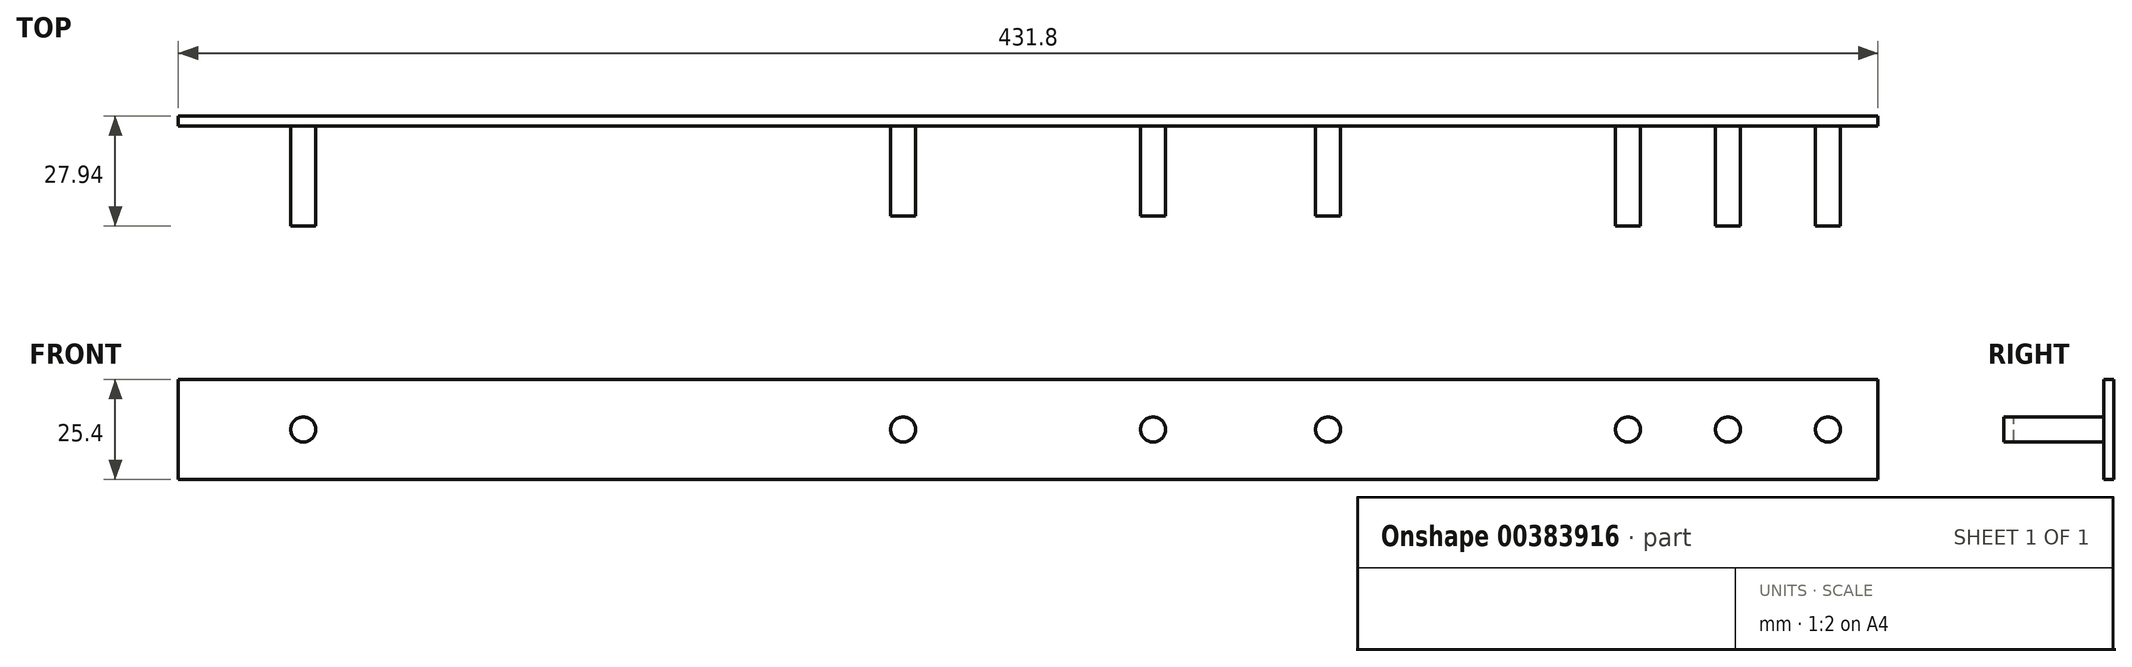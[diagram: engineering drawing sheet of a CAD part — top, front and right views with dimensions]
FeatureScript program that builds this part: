
annotation { "Feature Type Name" : "Feature", "Feature Type Description" : "" }
export const myFeature = defineFeature(function(context is Context, id is Id, definition is map)
    precondition{}
    {
        {
            var Q0;
            Q0=qCreatedBy(makeId("Front.planeOp"),FACE);
            var sketch = newSketch(context, id + "F0", { "sketchPlane" : qUnion([Q0])});
            skLineSegment(sketch, "E0.bottom", {"start": v(-88.9, 12.7) * mm, "end": v(88.9, 12.7) * mm});
            skLineSegment(sketch, "E0.top", {"start": v(-88.9, -12.7) * mm, "end": v(88.9, -12.7) * mm});
            skLineSegment(sketch, "E0.left", {"start": v(-88.9, 12.7) * mm, "end": v(-88.9, -12.7) * mm});
            skLineSegment(sketch, "E0.right", {"start": v(88.9, 12.7) * mm, "end": v(88.9, -12.7) * mm});
            skPoint(sketch, "E0.middle", {"position": v(0, 0) * mm});
            skSolve(sketch);
        }
        {
            var Q0;
            Q0=makeQuery(id+"F0.imprint","IMPRINT",FACE,{"disambiguationData":[TD([[makeQuery(id+"F0.imprint","IMPRINT",EDGE,{"derivedFrom":sQuery(id+"F0.wireOp",EDGE,"E0.bottom")}),-1.0]])]});
            extrude(context, id + "F1", {"entities" : qUnion([Q0]), "depth" : 2.54 * mm});
        }
        {
            var Q0;
            Q0=qCreatedBy(makeId("Front.planeOp"),FACE);
            var sketch = newSketch(context, id + "F2", { "sketchPlane" : qUnion([Q0])});
            skCircle(sketch, "E1", {"center": v(-31.75, 0) * mm, "radius": 3.18 * mm});
            skCircle(sketch, "E2.MirrorC", {"center": v(31.75, 0) * mm, "radius": 3.18 * mm});
            skCircle(sketch, "E3", {"center": v(76.2, 0) * mm, "radius": 3.18 * mm});
            skLineSegment(sketch, "E4", {"start": v(-31.75, 0) * mm, "end": v(-31.75, 53.04) * mm, "construction": true});
            skSolve(sketch);
        }
        {
            var Q0;
            Q0=makeQuery(id+"F2.imprint","IMPRINT",FACE,{"disambiguationData":[TD([[makeQuery(id+"F2.imprint","IMPRINT",EDGE,{"derivedFrom":sQuery(id+"F2.wireOp",EDGE,"E1")}),1.0]])]});
            var Q1;
            Q1=makeQuery(id+"F2.imprint","IMPRINT",FACE,{"disambiguationData":[TD([[makeQuery(id+"F2.imprint","IMPRINT",EDGE,{"derivedFrom":sQuery(id+"F2.wireOp",EDGE,"E2.MirrorC")}),-1.0]])]});
            extrude(context, id + "F3", {"entities" : qUnion([Q0, Q1]), "operationType" : NewBodyOperationType.ADD, "depth" : 25.4 * mm});
        }
        {
            var Q0;
            Q0 = qSketchRegion(id + "F2", true);
            extrude(context, id + "F4", {"entities" : qUnion([Q0]), "operationType" : NewBodyOperationType.ADD, "depth" : 25.4 * mm});
        }
        {
            var Q0;
            Q0=makeQuery(id+"F1.opExtrude","SWEPT_FACE",FACE,{"disambiguationData":[OSD([sQuery(id+"F0.wireOp",EDGE,"E0.left")])]});
            extrude(context, id + "F5", {"entities" : qUnion([Q0]), "operationType" : NewBodyOperationType.ADD, "depth" : 127 * mm});
        }
        {
            var Q0;
            {var subQ0=sQuery(id+"F0.wireOp",EDGE,"E0.left");Q0=makeQuery(id+"F5.boolean.opBoolean","MERGE",FACE,{"derivedFrom":[makeQuery(id+"F1.opExtrude","CAP_FACE",FACE,{"disambiguationData":[OSD([sQuery(id+"F0.wireOp",EDGE,"E0.bottom"),sQuery(id+"F0.wireOp",EDGE,"E0.top"),subQ0,sQuery(id+"F0.wireOp",EDGE,"E0.right")])],"isStart":false}),makeQuery(id+"F5.opExtrude","SWEPT_FACE",FACE,{"disambiguationData":[OSD([subQ0]),TDD([makeQuery(id+"F1.opExtrude","CAP_EDGE",EDGE,{"disambiguationData":[OSD([subQ0])],"isStart":false})])]})]});}
            var sketch = newSketch(context, id + "F6", { "sketchPlane" : qUnion([Q0])});
            skCircle(sketch, "E5", {"center": v(-184.15, 0) * mm, "radius": 3.18 * mm});
            skSolve(sketch);
        }
        {
            var Q0;
            Q0=makeQuery(id+"F6.imprint","IMPRINT",FACE,{"disambiguationData":[TD([[makeQuery(id+"F6.imprint","IMPRINT",EDGE,{"derivedFrom":sQuery(id+"F6.wireOp",EDGE,"E5")}),1.0]])]});
            extrude(context, id + "F7", {"entities" : qUnion([Q0]), "operationType" : NewBodyOperationType.ADD, "depth" : 25.4 * mm});
        }
        {
            var Q0;
            Q0=makeQuery(id+"F1.opExtrude","SWEPT_FACE",FACE,{"disambiguationData":[OSD([sQuery(id+"F0.wireOp",EDGE,"E0.right")])]});
            extrude(context, id + "F8", {"entities" : qUnion([Q0]), "operationType" : NewBodyOperationType.ADD, "depth" : 127 * mm});
        }
        {
            var Q0;
            {var subQ0=sQuery(id+"F0.wireOp",EDGE,"E0.right");var subQ1=sQuery(id+"F0.wireOp",EDGE,"E0.left");Q0=makeQuery(id+"F8.boolean.opBoolean","MERGE",FACE,{"derivedFrom":[makeQuery(id+"F5.boolean.opBoolean","MERGE",FACE,{"derivedFrom":[makeQuery(id+"F1.opExtrude","CAP_FACE",FACE,{"disambiguationData":[OSD([sQuery(id+"F0.wireOp",EDGE,"E0.bottom"),sQuery(id+"F0.wireOp",EDGE,"E0.top"),subQ1,subQ0])],"isStart":false}),makeQuery(id+"F5.opExtrude","SWEPT_FACE",FACE,{"disambiguationData":[OSD([subQ1]),TDD([makeQuery(id+"F1.opExtrude","CAP_EDGE",EDGE,{"disambiguationData":[OSD([subQ1])],"isStart":false})])]})]}),makeQuery(id+"F8.opExtrude","SWEPT_FACE",FACE,{"disambiguationData":[OSD([subQ0]),TDD([makeQuery(id+"F1.opExtrude","CAP_EDGE",EDGE,{"disambiguationData":[OSD([subQ0])],"isStart":false})])]})]});}
            var sketch = newSketch(context, id + "F9", { "sketchPlane" : qUnion([Q0])});
            skCircle(sketch, "E6", {"center": v(152.4, 0) * mm, "radius": 3.18 * mm});
            skCircle(sketch, "E7", {"center": v(177.8, 0) * mm, "radius": 3.18 * mm});
            skCircle(sketch, "E8", {"center": v(203.2, 0) * mm, "radius": 3.18 * mm});
            skSolve(sketch);
        }
        {
            var Q0;
            Q0=makeQuery(id+"F9.imprint","IMPRINT",FACE,{"disambiguationData":[TD([[makeQuery(id+"F9.imprint","IMPRINT",EDGE,{"derivedFrom":sQuery(id+"F9.wireOp",EDGE,"E6")}),1.0]])]});
            var Q1;
            Q1=makeQuery(id+"F9.imprint","IMPRINT",FACE,{"disambiguationData":[TD([[makeQuery(id+"F9.imprint","IMPRINT",EDGE,{"derivedFrom":sQuery(id+"F9.wireOp",EDGE,"E7")}),1.0]])]});
            var Q2;
            Q2=makeQuery(id+"F9.imprint","IMPRINT",FACE,{"disambiguationData":[TD([[makeQuery(id+"F9.imprint","IMPRINT",EDGE,{"derivedFrom":sQuery(id+"F9.wireOp",EDGE,"E8")}),1.0]])]});
            extrude(context, id + "F10", {"entities" : qUnion([Q0, Q1, Q2]), "operationType" : NewBodyOperationType.ADD, "depth" : 25.4 * mm});
        }
    });
